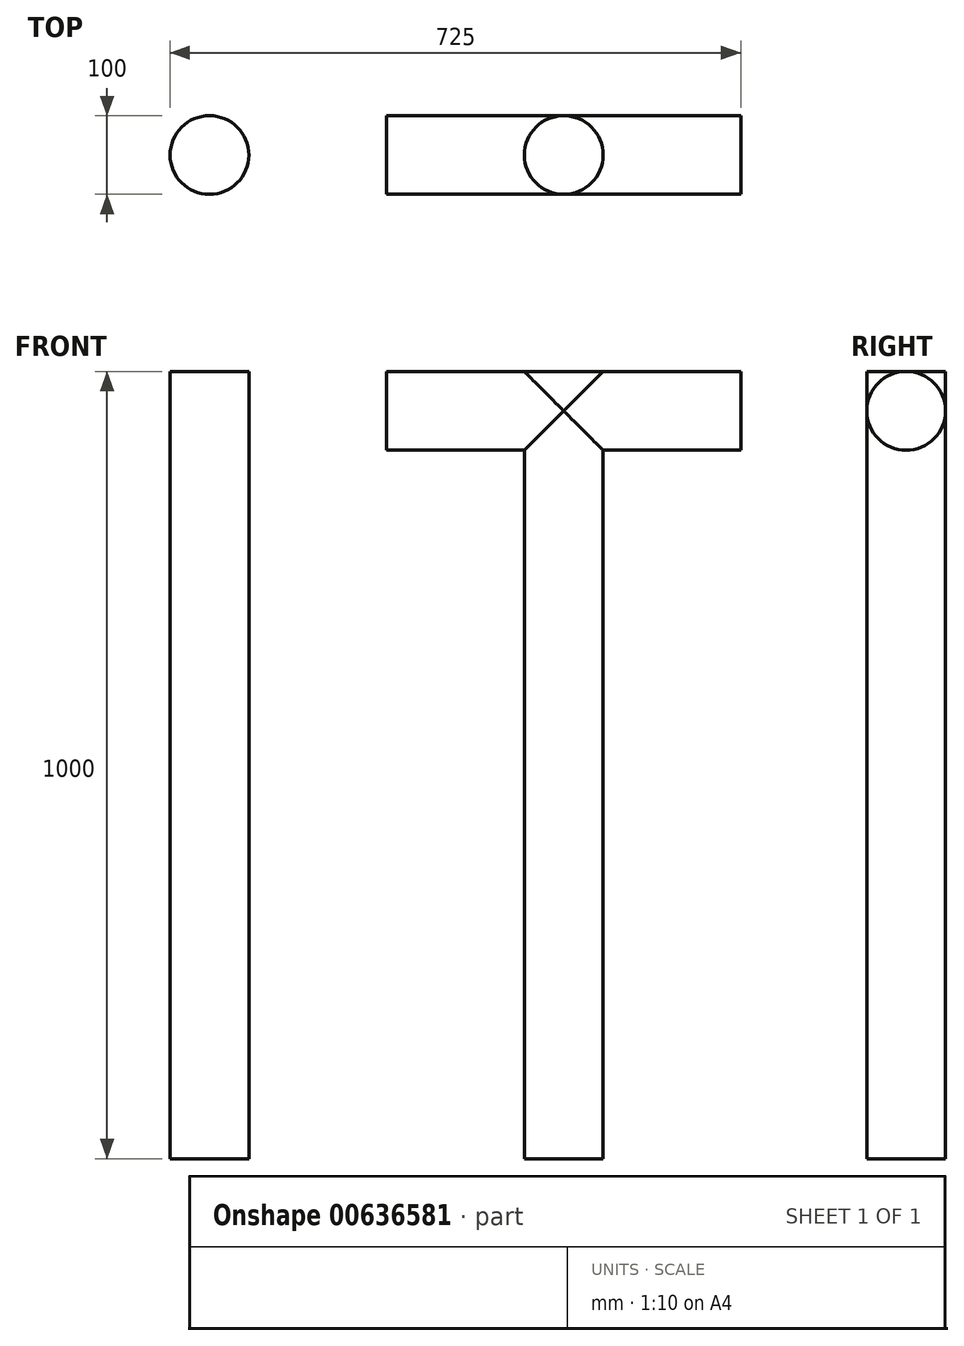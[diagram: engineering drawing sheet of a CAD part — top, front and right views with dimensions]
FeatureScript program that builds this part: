
annotation { "Feature Type Name" : "Feature", "Feature Type Description" : "" }
export const myFeature = defineFeature(function(context is Context, id is Id, definition is map)
    precondition{}
    {
        {
            var Q0;
            Q0=qCreatedBy(makeId("Top.planeOp"),FACE);
            var sketch = newSketch(context, id + "F0", { "sketchPlane" : qUnion([Q0])});
            skCircle(sketch, "E0", {"center": v(225, 0) * mm, "radius": 50 * mm});
            skCircle(sketch, "E1", {"center": v(-225, 0) * mm, "radius": 50 * mm});
            skSolve(sketch);
        }
        {
            var Q0;
            Q0 = qSketchRegion(id + "F0", true);
            extrude(context, id + "F1", {"entities" : qUnion([Q0]), "depth" : 1000 * mm, "offsetDistance" : 25 * mm});
        }
        {
            var Q0;
            Q0=qCreatedBy(makeId("Right.planeOp"),FACE);
            var sketch = newSketch(context, id + "F2", { "sketchPlane" : qUnion([Q0])});
            skCircle(sketch, "E2", {"center": v(0, 950) * mm, "radius": 50 * mm});
            skSolve(sketch);
        }
        {
            var Q0;
            Q0=makeQuery(id+"F2.imprint","IMPRINT",FACE,{"disambiguationData":[TD([[makeQuery(id+"F2.imprint","IMPRINT",EDGE,{"derivedFrom":sQuery(id+"F2.wireOp",EDGE,"E2")}),1.0]])]});
            extrude(context, id + "F3", {"entities" : qUnion([Q0]), "operationType" : NewBodyOperationType.ADD, "depth" : 450 * mm, "offsetDistance" : 25 * mm});
        }
    });
